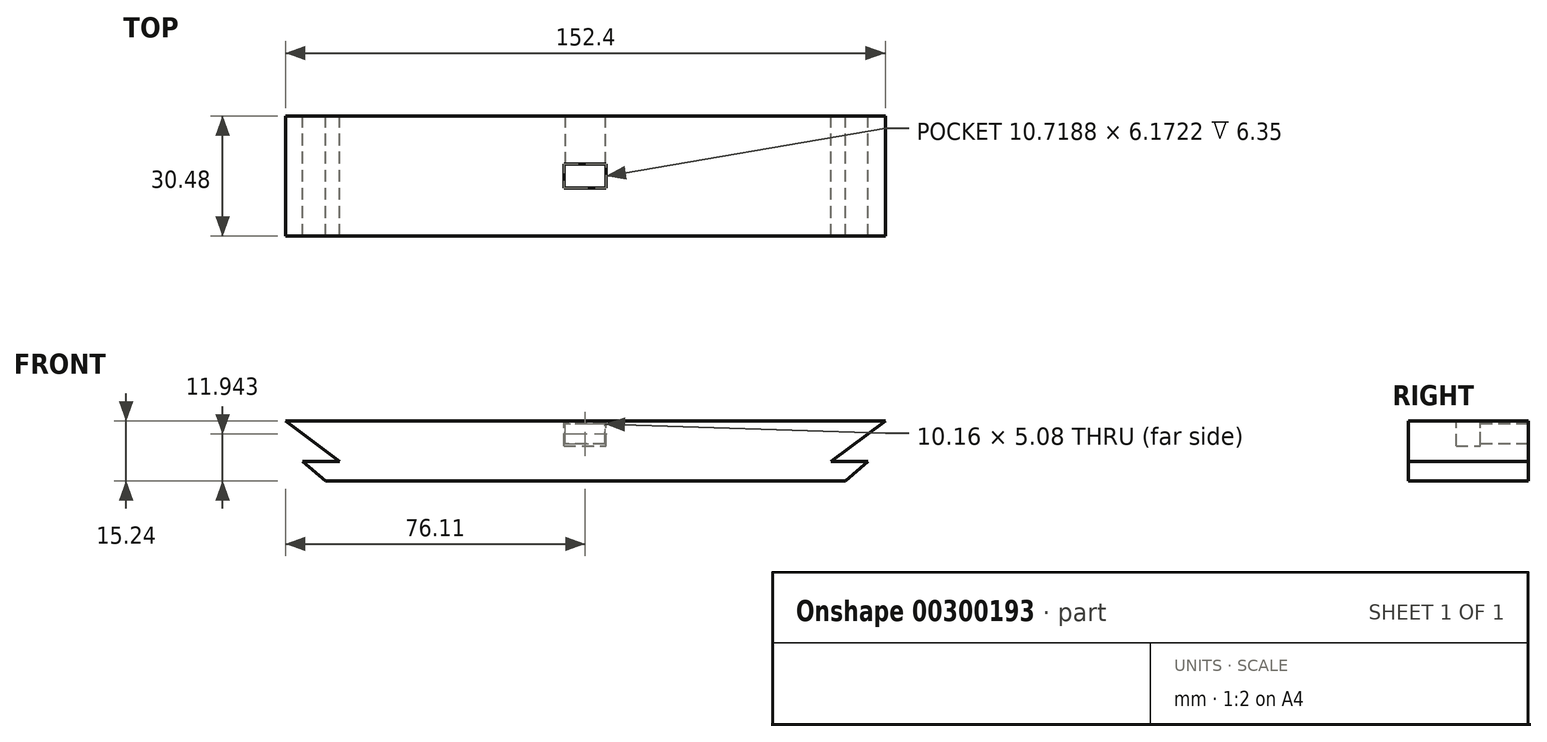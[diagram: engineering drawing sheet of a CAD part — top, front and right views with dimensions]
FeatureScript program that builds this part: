
annotation { "Feature Type Name" : "Feature", "Feature Type Description" : "" }
export const myFeature = defineFeature(function(context is Context, id is Id, definition is map)
    precondition{}
    {
        {
            var Q0;
            Q0=qCreatedBy(makeId("Front.planeOp"),FACE);
            var sketch = newSketch(context, id + "F0", { "sketchPlane" : qUnion([Q0])});
            skLineSegment(sketch, "E0", {"start": v(-76.1, 0) * mm, "end": v(76.3, 0) * mm});
            skLineSegment(sketch, "E1", {"start": v(76.3, 0) * mm, "end": v(55.97, -15.24) * mm});
            skLineSegment(sketch, "E2", {"start": v(-76.1, 0) * mm, "end": v(-55.79, -15.24) * mm});
            skLineSegment(sketch, "E3", {"start": v(-55.79, -15.24) * mm, "end": v(55.97, -15.24) * mm});
            skSolve(sketch);
        }
        {
            var Q0;
            Q0=makeQuery(id+"F0.imprint","IMPRINT",FACE,{"disambiguationData":[TD([[makeQuery(id+"F0.imprint","IMPRINT",EDGE,{"derivedFrom":sQuery(id+"F0.wireOp",EDGE,"E0")}),-1.0]])]});
            extrude(context, id + "F1", {"entities" : qUnion([Q0]), "depth" : 30.48 * mm});
        }
        {
            var Q0;
            Q0=makeQuery(id+"F1.opExtrude","SWEPT_FACE",FACE,{"disambiguationData":[OSD([sQuery(id+"F0.wireOp",EDGE,"E0")])]});
            var sketch = newSketch(context, id + "F2", { "sketchPlane" : qUnion([Q0])});
            skLineSegment(sketch, "E4.bottom", {"start": v(-5.36, -18.33) * mm, "end": v(5.36, -18.33) * mm});
            skLineSegment(sketch, "E4.top", {"start": v(-5.36, -12.15) * mm, "end": v(5.36, -12.15) * mm});
            skLineSegment(sketch, "E4.left", {"start": v(-5.36, -18.33) * mm, "end": v(-5.36, -12.15) * mm});
            skLineSegment(sketch, "E4.right", {"start": v(5.36, -18.33) * mm, "end": v(5.36, -12.15) * mm});
            skPoint(sketch, "E4.middle", {"position": v(0, -15.24) * mm});
            skSolve(sketch);
        }
        {
            var Q0;
            Q0=makeQuery(id+"F2.imprint","IMPRINT",FACE,{"disambiguationData":[TD([[makeQuery(id+"F2.imprint","IMPRINT",EDGE,{"derivedFrom":sQuery(id+"F2.wireOp",EDGE,"E4.bottom")}),1.0]])]});
            extrude(context, id + "F3", {"entities" : qUnion([Q0]), "operationType" : NewBodyOperationType.REMOVE, "oppositeDirection" : true, "depth" : 6.35 * mm});
        }
        {
            var Q0;
            Q0=makeQuery(id+"F3.boolean.opBoolean","COPY",FACE,{"derivedFrom":makeQuery(id+"F3.opExtrude","SWEPT_FACE",FACE,{"disambiguationData":[OSD([sQuery(id+"F2.wireOp",EDGE,"E4.top")])]})});
            var sketch = newSketch(context, id + "F4", { "sketchPlane" : qUnion([Q0])});
            skLineSegment(sketch, "E5.bottom", {"start": v(5.08, -5.84) * mm, "end": v(-5.08, -5.84) * mm});
            skLineSegment(sketch, "E5.top", {"start": v(5.08, -0.76) * mm, "end": v(-5.08, -0.76) * mm});
            skLineSegment(sketch, "E5.left", {"start": v(5.08, -5.84) * mm, "end": v(5.08, -0.76) * mm});
            skLineSegment(sketch, "E5.right", {"start": v(-5.08, -5.84) * mm, "end": v(-5.08, -0.76) * mm});
            skPoint(sketch, "E5.middle", {"position": v(0, -3.3) * mm});
            skSolve(sketch);
        }
        {
            var Q0;
            Q0=makeQuery(id+"F4.imprint","IMPRINT",FACE,{"disambiguationData":[TD([[makeQuery(id+"F4.imprint","IMPRINT",EDGE,{"derivedFrom":sQuery(id+"F4.wireOp",EDGE,"E5.bottom")}),-1.0]])]});
            extrude(context, id + "F5", {"entities" : qUnion([Q0]), "operationType" : NewBodyOperationType.REMOVE, "oppositeDirection" : true, "depth" : 25.4 * mm});
        }
        {
            var Q0;
            Q0=makeQuery(id+"F1.opExtrude","CAP_FACE",FACE,{"disambiguationData":[OSD([sQuery(id+"F0.wireOp",EDGE,"E0"),sQuery(id+"F0.wireOp",EDGE,"E1"),sQuery(id+"F0.wireOp",EDGE,"E2"),sQuery(id+"F0.wireOp",EDGE,"E3")])],"isStart":true});
            var sketch = newSketch(context, id + "F6", { "sketchPlane" : qUnion([Q0])});
            skLineSegment(sketch, "E6", {"start": v(-62.54, -10.31) * mm, "end": v(-71.94, -10.31) * mm});
            skLineSegment(sketch, "E7", {"start": v(-71.94, -10.31) * mm, "end": v(-66.13, -15.24) * mm});
            skLineSegment(sketch, "E8", {"start": v(-66.13, -15.24) * mm, "end": v(-55.97, -15.24) * mm});
            skLineSegment(sketch, "E9", {"start": v(-55.97, -15.24) * mm, "end": v(-62.54, -10.31) * mm});
            skLineSegment(sketch, "E10", {"start": v(55.79, -15.24) * mm, "end": v(65.95, -15.24) * mm});
            skLineSegment(sketch, "E11", {"start": v(65.95, -15.24) * mm, "end": v(71.76, -10.31) * mm});
            skLineSegment(sketch, "E12", {"start": v(71.76, -10.31) * mm, "end": v(62.36, -10.31) * mm});
            skLineSegment(sketch, "E13", {"start": v(62.36, -10.31) * mm, "end": v(55.79, -15.24) * mm});
            skSolve(sketch);
        }
        {
            var Q0;
            Q0=makeQuery(id+"F6.imprint","IMPRINT",FACE,{"disambiguationData":[TD([[makeQuery(id+"F6.imprint","IMPRINT",EDGE,{"derivedFrom":sQuery(id+"F6.wireOp",EDGE,"E10")}),1.0]])]});
            var Q1;
            Q1=makeQuery(id+"F6.imprint","IMPRINT",FACE,{"disambiguationData":[TD([[makeQuery(id+"F6.imprint","IMPRINT",EDGE,{"derivedFrom":sQuery(id+"F6.wireOp",EDGE,"E6")}),1.0]])]});
            extrude(context, id + "F7", {"entities" : qUnion([Q0, Q1]), "operationType" : NewBodyOperationType.ADD, "oppositeDirection" : true, "depth" : 30.48 * mm});
        }
    });
